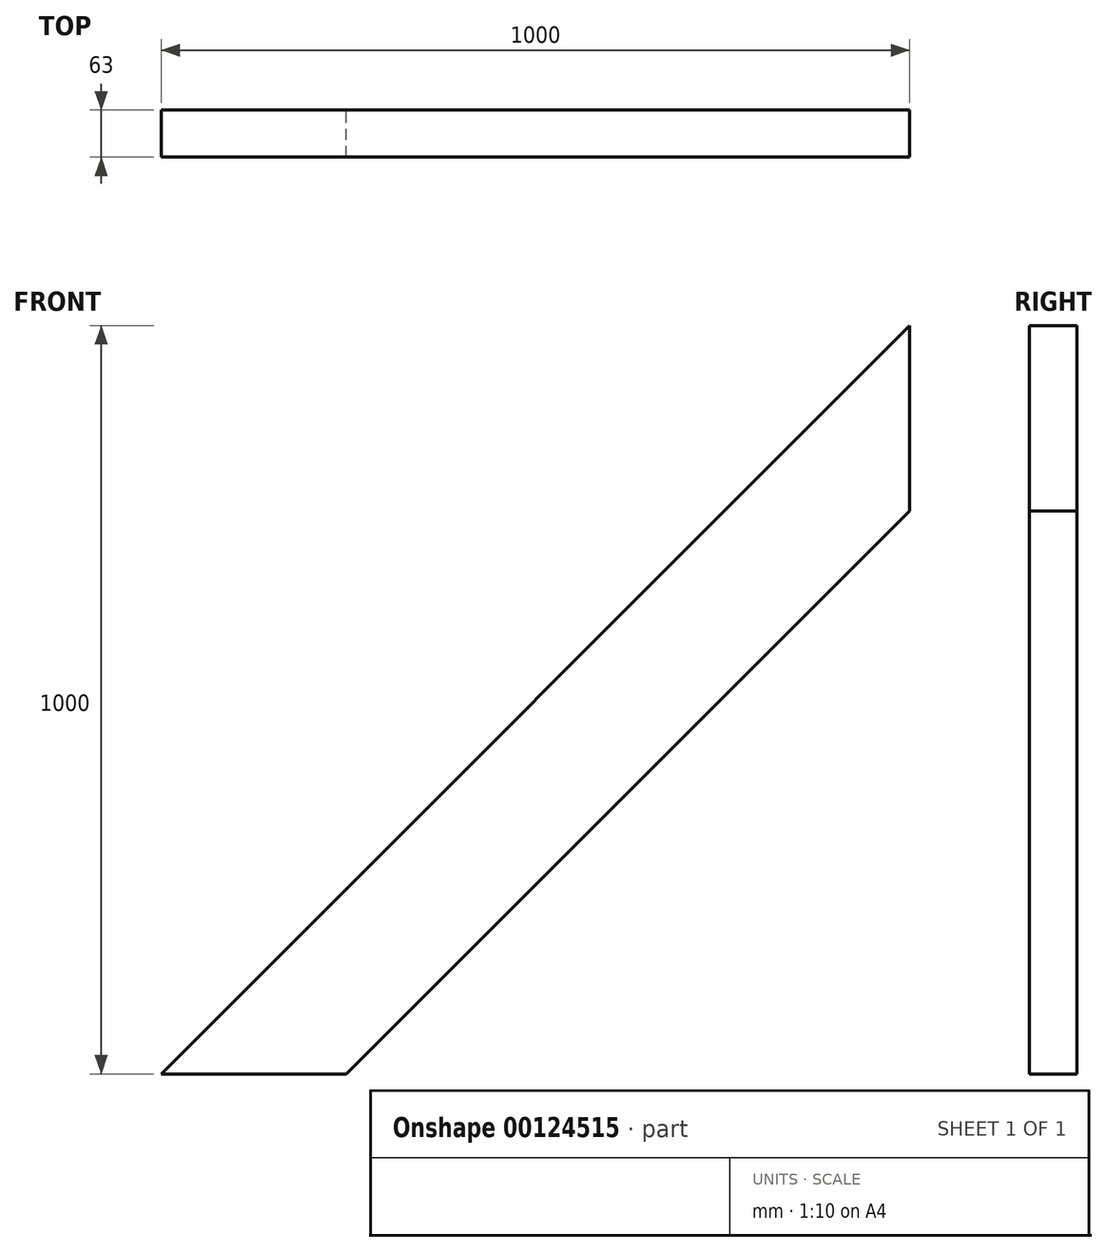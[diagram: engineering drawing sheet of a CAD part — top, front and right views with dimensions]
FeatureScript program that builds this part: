
annotation { "Feature Type Name" : "Feature", "Feature Type Description" : "" }
export const myFeature = defineFeature(function(context is Context, id is Id, definition is map)
    precondition{}
    {
        {
            var Q0;
            Q0=qCreatedBy(makeId("Front.planeOp"),FACE);
            var sketch = newSketch(context, id + "F0", { "sketchPlane" : qUnion([Q0])});
            skLineSegment(sketch, "E0", {"start": v(-644.12, 0) * mm, "end": v(-396.63, 0) * mm});
            skLineSegment(sketch, "E1", {"start": v(-396.63, 0) * mm, "end": v(355.88, 752.51) * mm});
            skLineSegment(sketch, "E2", {"start": v(355.88, 752.51) * mm, "end": v(355.88, 1000) * mm});
            skLineSegment(sketch, "E3", {"start": v(355.88, 1000) * mm, "end": v(-644.12, 0) * mm});
            skSolve(sketch);
        }
        {
            var Q0;
            Q0=qSketchRegion(id+"F0",true);
            extrude(context, id + "F1", {"entities" : qUnion([Q0]), "depth" : 63 * mm});
        }
    });
